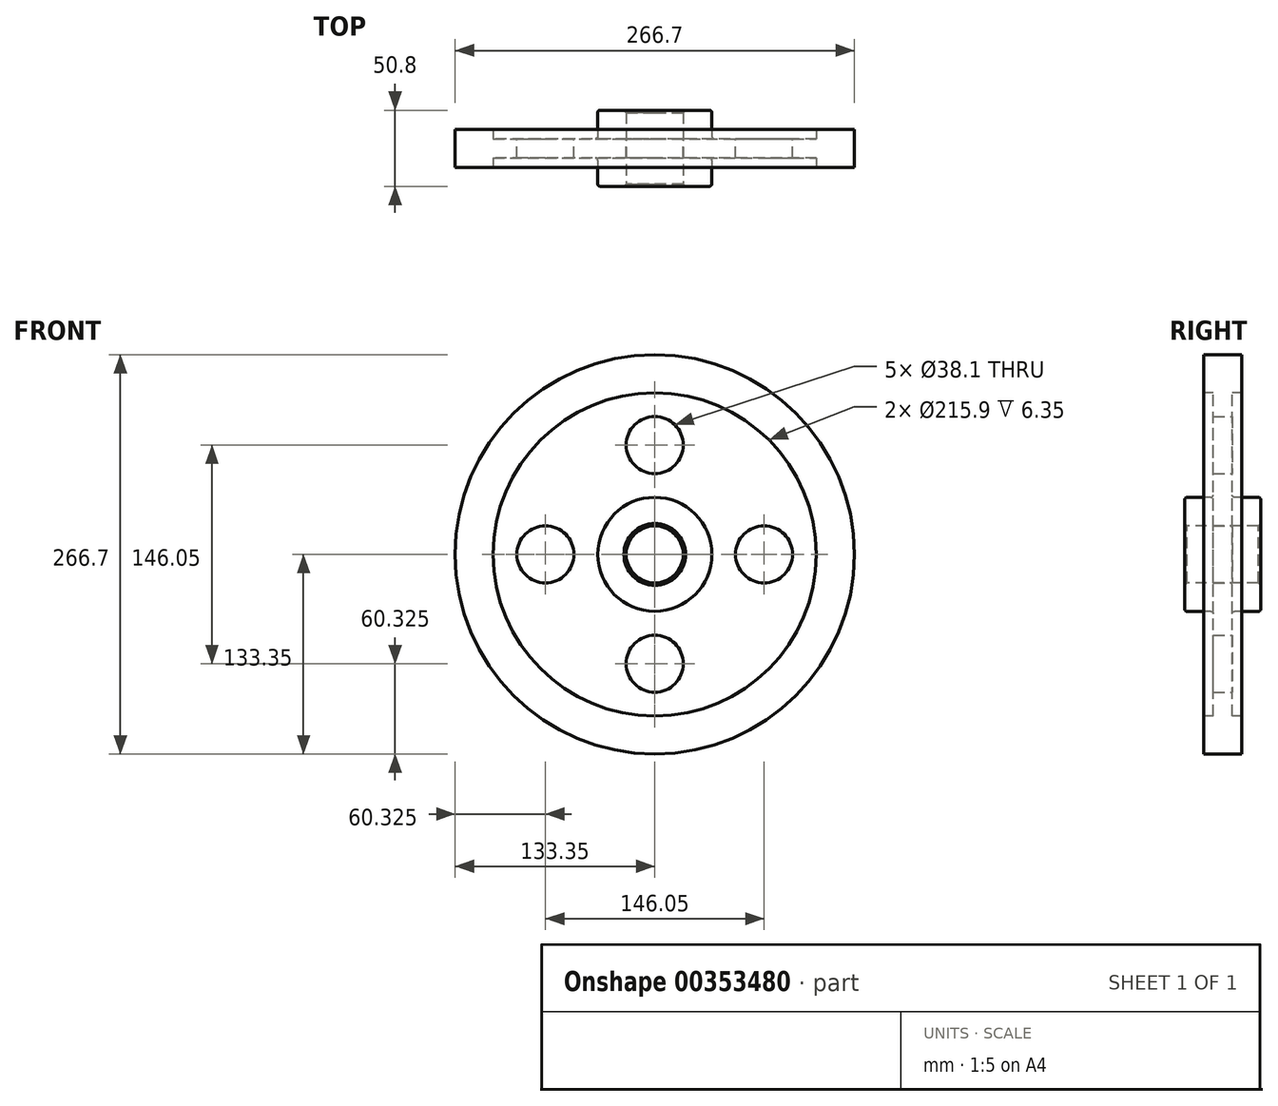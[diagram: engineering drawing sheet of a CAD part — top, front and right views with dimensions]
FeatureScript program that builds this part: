
annotation { "Feature Type Name" : "Feature", "Feature Type Description" : "" }
export const myFeature = defineFeature(function(context is Context, id is Id, definition is map)
    precondition{}
    {
        {
            var Q0;
            Q0=qCreatedBy(makeId("Right.planeOp"),FACE);
            var sketch = newSketch(context, id + "F0", { "sketchPlane" : qUnion([Q0])});
            skLineSegment(sketch, "E0", {"start": v(0, 0) * mm, "end": v(97, 0) * mm, "construction": true});
            skLineSegment(sketch, "E1.0", {"start": v(0, 19.05) * mm, "end": v(25.4, 19.05) * mm});
            skLineSegment(sketch, "E2.0", {"start": v(6.35, 38.1) * mm, "end": v(25.4, 38.1) * mm});
            skLineSegment(sketch, "E3.0", {"start": v(6.35, 107.95) * mm, "end": v(12.7, 107.95) * mm});
            skLineSegment(sketch, "E4.0", {"start": v(0, 133.35) * mm, "end": v(12.7, 133.35) * mm});
            skLineSegment(sketch, "E5", {"start": v(0, 0) * mm, "end": v(0, 133.35) * mm, "construction": true});
            skLineSegment(sketch, "E6.0", {"start": v(25.4, 19.05) * mm, "end": v(25.4, 38.1) * mm});
            skLineSegment(sketch, "E7.0", {"start": v(6.35, 38.1) * mm, "end": v(6.35, 107.95) * mm});
            skLineSegment(sketch, "E8.trimOffspring", {"start": v(12.7, 107.95) * mm, "end": v(12.7, 133.35) * mm});
            skLineSegment(sketch, "E9.MirrorCS", {"start": v(0, 133.35) * mm, "end": v(-12.7, 133.35) * mm});
            skLineSegment(sketch, "E10.MirrorCS", {"start": v(-12.7, 107.95) * mm, "end": v(-12.7, 133.35) * mm});
            skLineSegment(sketch, "E11.MirrorCS", {"start": v(-6.35, 38.1) * mm, "end": v(-6.35, 107.95) * mm});
            skLineSegment(sketch, "E12.MirrorCS", {"start": v(-6.35, 107.95) * mm, "end": v(-12.7, 107.95) * mm});
            skLineSegment(sketch, "E13.MirrorCS", {"start": v(-6.35, 38.1) * mm, "end": v(-25.4, 38.1) * mm});
            skLineSegment(sketch, "E14.MirrorCS", {"start": v(-25.4, 19.05) * mm, "end": v(-25.4, 38.1) * mm});
            skLineSegment(sketch, "E15.MirrorCS", {"start": v(0, 19.05) * mm, "end": v(-25.4, 19.05) * mm});
            skSolve(sketch);
        }
        {
            var Q0;
            Q0=makeQuery(id+"F0.imprint","IMPRINT",FACE,{"disambiguationData":[TD([[makeQuery(id+"F0.imprint","IMPRINT",EDGE,{"derivedFrom":sQuery(id+"F0.wireOp",EDGE,"E1.0")}),1.0]])]});
            var Q1;
            Q1=sQuery(id+"F0.wireOp",EDGE,"E0");
            revolve(context, id + "F1", {"entities" : qUnion([Q0]), "axis" : qUnion([Q1]), "revolveType" : RevolveType.FULL});
        }
        {
            var Q0;
            Q0=makeQuery(id+"F1.opRevolve","SWEPT_FACE",FACE,{"disambiguationData":[OSD([sQuery(id+"F0.wireOp",EDGE,"E7.0")])]});
            var sketch = newSketch(context, id + "F2", { "sketchPlane" : qUnion([Q0])});
            skLineSegment(sketch, "E16", {"start": v(0, 0) * mm, "end": v(0, 73.03) * mm});
            skCircle(sketch, "E17", {"center": v(0, 73.03) * mm, "radius": 19.05 * mm});
            skCircle(sketch, "E18.1.0", {"center": v(-73.03, 0) * mm, "radius": 19.05 * mm});
            skCircle(sketch, "E18.2.0", {"center": v(0, -73.03) * mm, "radius": 19.05 * mm});
            skCircle(sketch, "E18.3.0", {"center": v(73.03, 0) * mm, "radius": 19.05 * mm});
            skPoint(sketch, "E18.center", {"position": v(0, 0) * mm});
            skSolve(sketch);
        }
        {
            var Q0;
            Q0=makeQuery(id+"F2.imprint","IMPRINT",FACE,{"disambiguationData":[TD([[makeQuery(id+"F2.imprint","IMPRINT",EDGE,{"derivedFrom":sQuery(id+"F2.wireOp",EDGE,"E18.3.0")}),1.0]])]});
            var Q1;
            Q1=makeQuery(id+"F2.imprint","IMPRINT",FACE,{"disambiguationData":[TD([[makeQuery(id+"F2.imprint","IMPRINT",EDGE,{"derivedFrom":sQuery(id+"F2.wireOp",EDGE,"E18.2.0")}),1.0]])]});
            var Q2;
            Q2=makeQuery(id+"F2.imprint","IMPRINT",FACE,{"disambiguationData":[TD([[makeQuery(id+"F2.imprint","IMPRINT",EDGE,{"derivedFrom":sQuery(id+"F2.wireOp",EDGE,"E18.1.0")}),1.0]])]});
            var Q3;
            Q3=makeQuery(id+"F2.imprint","IMPRINT",FACE,{"disambiguationData":[TD([[makeQuery(id+"F2.imprint","IMPRINT",EDGE,{"derivedFrom":sQuery(id+"F2.wireOp",EDGE,"E17")}),1.0]])]});
            extrude(context, id + "F3", {"entities" : qUnion([Q0, Q1, Q2, Q3]), "operationType" : NewBodyOperationType.REMOVE, "oppositeDirection" : true, "depth" : 25.4 * mm});
        }
        {
            var Q0;
            Q0=makeQuery(id+"F1.opRevolve","SWEPT_EDGE",EDGE,{"disambiguationData":[OSD([sQuery(id+"F0.wireOp",EDGE,"E2.0"),sQuery(id+"F0.wireOp",EDGE,"E7.0")])]});
            var Q1;
            Q1=makeQuery(id+"F1.opRevolve","SWEPT_EDGE",EDGE,{"disambiguationData":[OSD([sQuery(id+"F0.wireOp",EDGE,"E2.0"),sQuery(id+"F0.wireOp",EDGE,"E6.0")])]});
            fillet(context, id + "F4", {"entities" : qUnion([Q0, Q1]), "radius" : 1.59 * mm, "tangentPropagation" : true, "allowEdgeOverflow" : false});
        }
        {
            var Q0;
            Q0=makeQuery(id+"F1.opRevolve","SWEPT_EDGE",EDGE,{"disambiguationData":[OSD([sQuery(id+"F0.wireOp",EDGE,"E11.MirrorCS"),sQuery(id+"F0.wireOp",EDGE,"E13.MirrorCS")])]});
            var Q1;
            Q1=makeQuery(id+"F1.opRevolve","SWEPT_EDGE",EDGE,{"disambiguationData":[OSD([sQuery(id+"F0.wireOp",EDGE,"E13.MirrorCS"),sQuery(id+"F0.wireOp",EDGE,"E14.MirrorCS")])]});
            fillet(context, id + "F5", {"entities" : qUnion([Q0, Q1]), "radius" : 1.59 * mm, "tangentPropagation" : true, "allowEdgeOverflow" : false});
        }
        {
            var Q0;
            Q0=makeQuery(id+"F1.opRevolve","SWEPT_EDGE",EDGE,{"disambiguationData":[OSD([sQuery(id+"F0.wireOp",EDGE,"E14.MirrorCS"),sQuery(id+"F0.wireOp",EDGE,"E15.MirrorCS")])]});
            var Q1;
            Q1=makeQuery(id+"F1.opRevolve","SWEPT_EDGE",EDGE,{"disambiguationData":[OSD([sQuery(id+"F0.wireOp",EDGE,"E1.0"),sQuery(id+"F0.wireOp",EDGE,"E6.0")])]});
            chamfer(context, id + "F6", {"entities" : qUnion([Q0, Q1]), "width" : 1.59 * mm, "tangentPropagation" : true});
        }
    });
